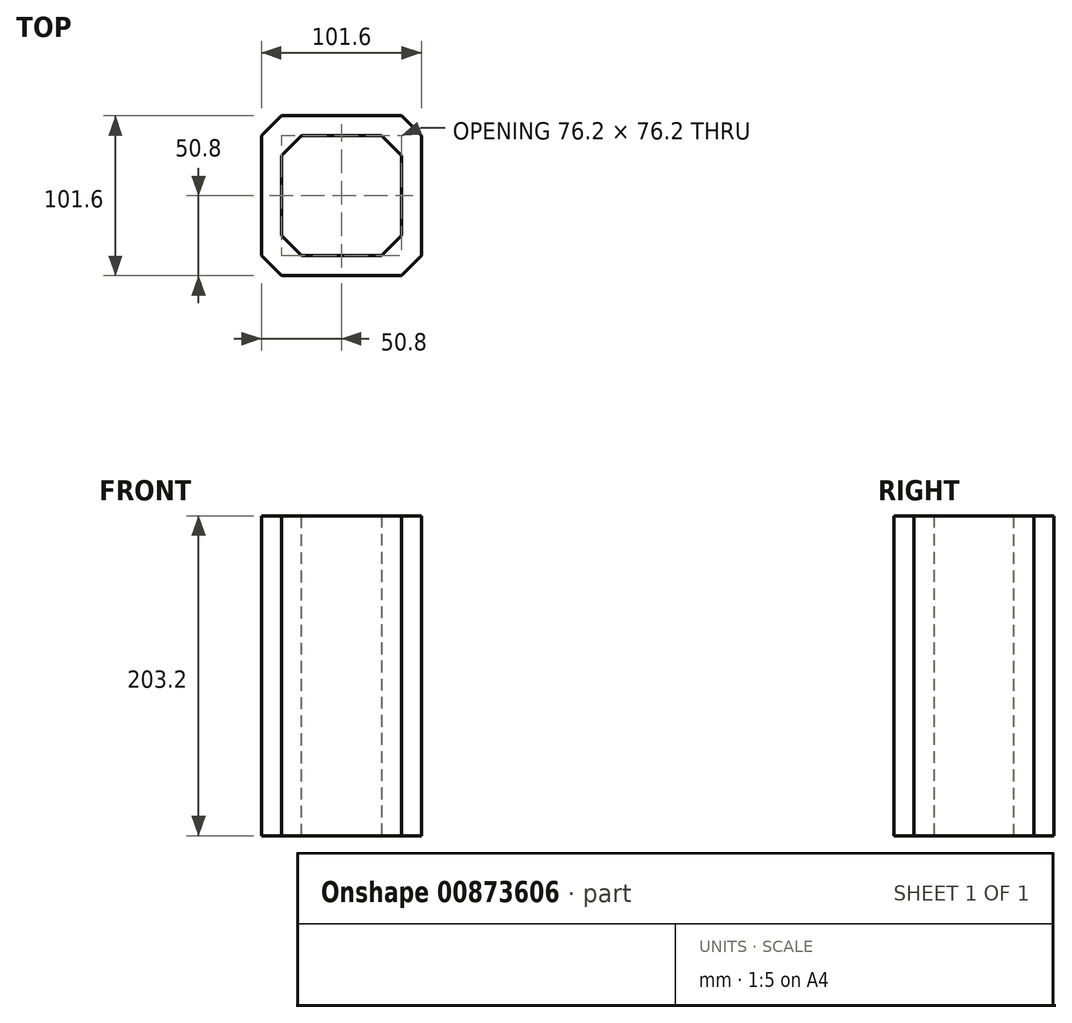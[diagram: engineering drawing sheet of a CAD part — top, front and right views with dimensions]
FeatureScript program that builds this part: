
annotation { "Feature Type Name" : "Feature", "Feature Type Description" : "" }
export const myFeature = defineFeature(function(context is Context, id is Id, definition is map)
    precondition{}
    {
        {
            var Q0;
            Q0=qCreatedBy(makeId("Top.planeOp"),FACE);
            var sketch = newSketch(context, id + "F0", { "sketchPlane" : qUnion([Q0])});
            skLineSegment(sketch, "E0.bottom", {"start": v(0, 0) * mm, "end": v(101.6, 0) * mm});
            skLineSegment(sketch, "E0.top", {"start": v(0, 101.6) * mm, "end": v(101.6, 101.6) * mm});
            skLineSegment(sketch, "E0.left", {"start": v(0, 0) * mm, "end": v(0, 101.6) * mm});
            skLineSegment(sketch, "E0.right", {"start": v(101.6, 0) * mm, "end": v(101.6, 101.6) * mm});
            skLineSegment(sketch, "E1.0", {"start": v(12.7, 12.7) * mm, "end": v(12.7, 88.9) * mm});
            skLineSegment(sketch, "E1.1", {"start": v(12.7, 12.7) * mm, "end": v(88.9, 12.7) * mm});
            skLineSegment(sketch, "E1.2", {"start": v(88.9, 12.7) * mm, "end": v(88.9, 88.9) * mm});
            skLineSegment(sketch, "E1.3", {"start": v(12.7, 88.9) * mm, "end": v(88.9, 88.9) * mm});
            skSolve(sketch);
        }
        {
            var Q0;
            Q0 = qSketchRegion(id + "F0", true);
            extrude(context, id + "F1", {"entities" : qUnion([Q0]), "depth" : 203.2 * mm, "offsetDistance" : 25.4 * mm});
        }
        {
            var Q0;
            Q0=makeQuery(id+"F1.opExtrude","SWEPT_EDGE",EDGE,{"disambiguationData":[OSD([sQuery(id+"F0.wireOp",EDGE,"E1.0"),sQuery(id+"F0.wireOp",EDGE,"E1.3")])]});
            var Q1;
            Q1=makeQuery(id+"F1.opExtrude","SWEPT_EDGE",EDGE,{"disambiguationData":[OSD([sQuery(id+"F0.wireOp",EDGE,"E1.2"),sQuery(id+"F0.wireOp",EDGE,"E1.3")])]});
            var Q2;
            Q2=makeQuery(id+"F1.opExtrude","SWEPT_EDGE",EDGE,{"disambiguationData":[OSD([sQuery(id+"F0.wireOp",EDGE,"E1.1"),sQuery(id+"F0.wireOp",EDGE,"E1.2")])]});
            var Q3;
            Q3=makeQuery(id+"F1.opExtrude","SWEPT_EDGE",EDGE,{"disambiguationData":[OSD([sQuery(id+"F0.wireOp",EDGE,"E1.0"),sQuery(id+"F0.wireOp",EDGE,"E1.1")])]});
            chamfer(context, id + "F2", {"entities" : qUnion([Q0, Q1, Q2, Q3]), "width" : 12.7 * mm, "tangentPropagation" : true});
        }
        {
            var Q0;
            Q0=makeQuery(id+"F1.opExtrude","SWEPT_EDGE",EDGE,{"disambiguationData":[OSD([sQuery(id+"F0.wireOp",EDGE,"E0.bottom"),sQuery(id+"F0.wireOp",EDGE,"E0.right")])]});
            var Q1;
            Q1=makeQuery(id+"F1.opExtrude","SWEPT_EDGE",EDGE,{"disambiguationData":[OSD([sQuery(id+"F0.wireOp",EDGE,"E0.top"),sQuery(id+"F0.wireOp",EDGE,"E0.right")])]});
            var Q2;
            Q2=makeQuery(id+"F1.opExtrude","SWEPT_EDGE",EDGE,{"disambiguationData":[OSD([sQuery(id+"F0.wireOp",EDGE,"E0.bottom"),sQuery(id+"F0.wireOp",EDGE,"E0.left")])]});
            var Q3;
            Q3=makeQuery(id+"F1.opExtrude","SWEPT_EDGE",EDGE,{"disambiguationData":[OSD([sQuery(id+"F0.wireOp",EDGE,"E0.top"),sQuery(id+"F0.wireOp",EDGE,"E0.left")])]});
            chamfer(context, id + "F3", {"entities" : qUnion([Q0, Q1, Q2, Q3]), "width" : 12.7 * mm, "tangentPropagation" : true});
        }
    });
